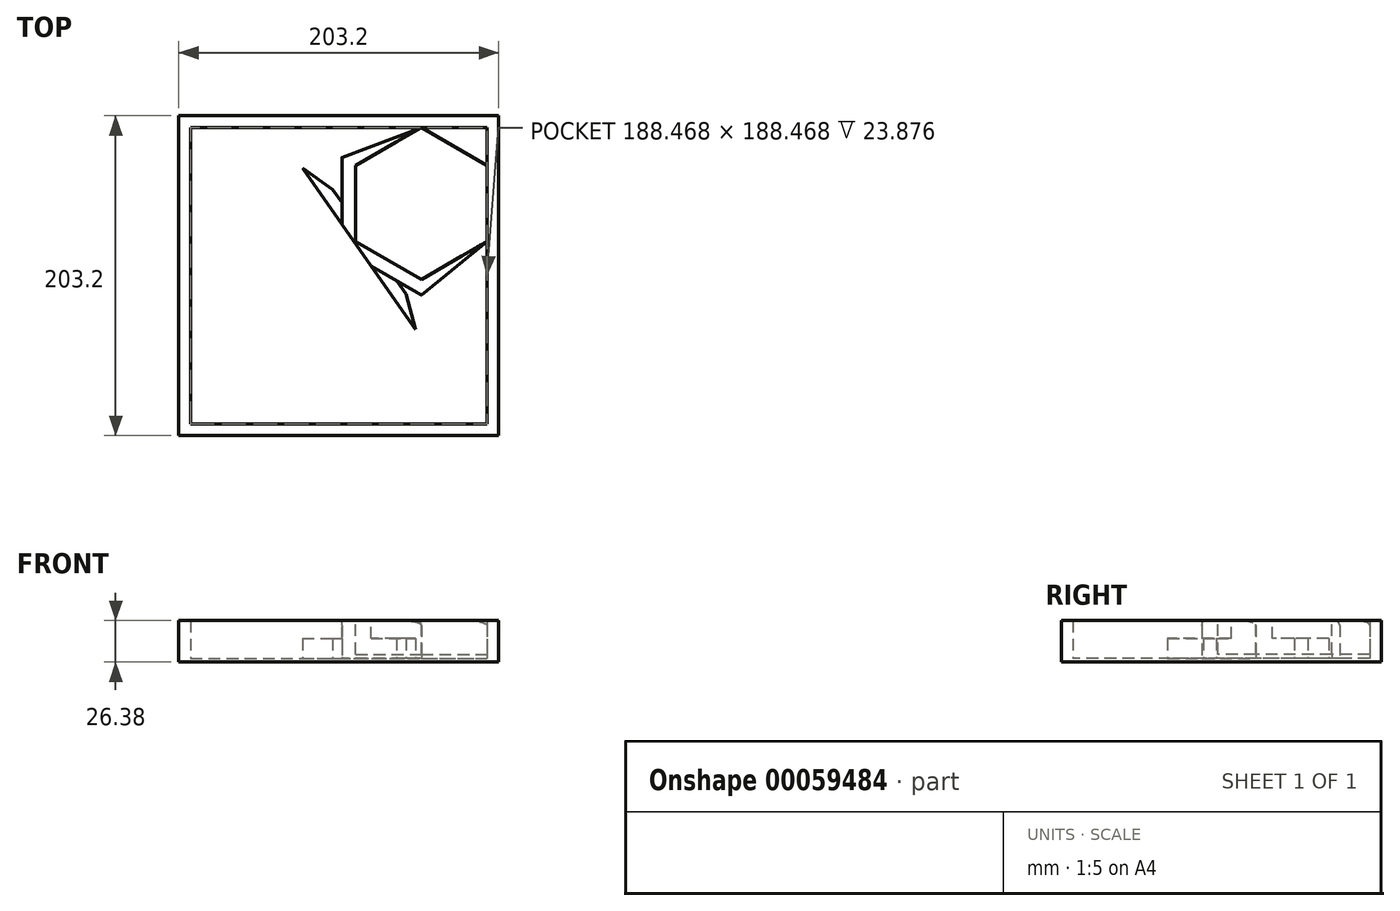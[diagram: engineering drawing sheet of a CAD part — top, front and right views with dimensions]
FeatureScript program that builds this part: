
annotation { "Feature Type Name" : "Feature", "Feature Type Description" : "" }
export const myFeature = defineFeature(function(context is Context, id is Id, definition is map)
    precondition{}
    {
        {
            var Q0;
            Q0=qCreatedBy(makeId("Top.planeOp"),FACE);
            var sketch = newSketch(context, id + "F0", { "sketchPlane" : qUnion([Q0])});
            skLineSegment(sketch, "E0.bottom", {"start": v(0, 0) * mm, "end": v(203.2, 0) * mm});
            skLineSegment(sketch, "E0.top", {"start": v(0, 203.2) * mm, "end": v(203.2, 203.2) * mm});
            skLineSegment(sketch, "E0.left", {"start": v(0, 0) * mm, "end": v(0, 203.2) * mm});
            skLineSegment(sketch, "E0.right", {"start": v(203.2, 0) * mm, "end": v(203.2, 203.2) * mm});
            skSolve(sketch);
        }
        {
            var Q0;
            Q0 = qSketchRegion(id + "F0", true);
            extrude(context, id + "F1", {"entities" : qUnion([Q0]), "depth" : 2.5 * mm});
        }
        {
            var Q0;
            Q0=makeQuery(id+"F1.opExtrude","CAP_FACE",FACE,{"disambiguationData":[OSD([sQuery(id+"F0.wireOp",EDGE,"E0.bottom"),sQuery(id+"F0.wireOp",EDGE,"E0.top"),sQuery(id+"F0.wireOp",EDGE,"E0.left"),sQuery(id+"F0.wireOp",EDGE,"E0.right")])],"isStart":false});
            var sketch = newSketch(context, id + "F2", { "sketchPlane" : qUnion([Q0])});
            skLineSegment(sketch, "E1.bottom", {"start": v(0, 203.2) * mm, "end": v(203.2, 203.2) * mm});
            skLineSegment(sketch, "E1.top", {"start": v(0, 0) * mm, "end": v(203.2, 0) * mm});
            skLineSegment(sketch, "E1.left", {"start": v(0, 203.2) * mm, "end": v(0, 0) * mm});
            skLineSegment(sketch, "E1.right", {"start": v(203.2, 203.2) * mm, "end": v(203.2, 0) * mm});
            skLineSegment(sketch, "E2.bottom", {"start": v(7.37, 195.83) * mm, "end": v(195.83, 195.83) * mm});
            skLineSegment(sketch, "E2.top", {"start": v(7.37, 7.37) * mm, "end": v(195.83, 7.37) * mm});
            skLineSegment(sketch, "E2.left", {"start": v(7.37, 195.83) * mm, "end": v(7.37, 7.37) * mm});
            skLineSegment(sketch, "E2.right", {"start": v(195.83, 195.83) * mm, "end": v(195.83, 7.37) * mm});
            skSolve(sketch);
        }
        {
            var Q0;
            Q0 = qSketchRegion(id + "F2", true);
            extrude(context, id + "F3", {"entities" : qUnion([Q0]), "operationType" : NewBodyOperationType.ADD, "depth" : 23.88 * mm});
        }
        {
            var Q0;
            Q0=makeQuery(id+"F1.opExtrude","CAP_FACE",FACE,{"disambiguationData":[OSD([sQuery(id+"F0.wireOp",EDGE,"E0.bottom"),sQuery(id+"F0.wireOp",EDGE,"E0.top"),sQuery(id+"F0.wireOp",EDGE,"E0.left"),sQuery(id+"F0.wireOp",EDGE,"E0.right")])],"isStart":false});
            var sketch = newSketch(context, id + "F4", { "sketchPlane" : qUnion([Q0])});
            skCircle(sketch, "E3.cCircle", {"center": v(154.04, 147.57) * mm, "radius": 41.8 * mm, "construction": true});
            skLineSegment(sketch, "E3.0", {"start": v(195.83, 171.7) * mm, "end": v(195.83, 123.44) * mm});
            skLineSegment(sketch, "E3.1", {"start": v(195.83, 123.44) * mm, "end": v(154.04, 99.31) * mm, "construction": true});
            skLineSegment(sketch, "E3.2", {"start": v(154.04, 99.31) * mm, "end": v(112.25, 123.44) * mm, "construction": true});
            skLineSegment(sketch, "E3.3", {"start": v(112.25, 123.44) * mm, "end": v(112.25, 171.7) * mm, "construction": true});
            skLineSegment(sketch, "E3.4", {"start": v(112.25, 171.7) * mm, "end": v(154.04, 195.83) * mm, "construction": true});
            skLineSegment(sketch, "E3.5", {"start": v(154.04, 195.83) * mm, "end": v(195.83, 171.7) * mm});
            skPoint(sketch, "E3.0.midPoint", {"position": v(195.83, 147.57) * mm});
            skLineSegment(sketch, "E4", {"start": v(154.04, 195.83) * mm, "end": v(103.58, 176.7) * mm});
            skLineSegment(sketch, "E5", {"start": v(103.58, 176.7) * mm, "end": v(112.25, 123.44) * mm, "construction": true});
            skLineSegment(sketch, "E6", {"start": v(112.25, 123.44) * mm, "end": v(154.04, 89.31) * mm, "construction": true});
            skLineSegment(sketch, "E7", {"start": v(154.04, 89.31) * mm, "end": v(195.83, 123.44) * mm});
            skLineSegment(sketch, "E8", {"start": v(78.53, 169.85) * mm, "end": v(150.23, 67.46) * mm});
            skLineSegment(sketch, "E9", {"start": v(195.83, 7.37) * mm, "end": v(7.37, 7.37) * mm, "construction": true});
            skLineSegment(sketch, "E10", {"start": v(7.37, 7.37) * mm, "end": v(7.37, 195.83) * mm, "construction": true});
            skLineSegment(sketch, "E11", {"start": v(78.53, 169.85) * mm, "end": v(97.69, 156.44) * mm});
            skLineSegment(sketch, "E12", {"start": v(97.69, 156.44) * mm, "end": v(109.66, 139.34) * mm});
            skLineSegment(sketch, "E13", {"start": v(150.23, 67.46) * mm, "end": v(144.17, 90.05) * mm});
            skLineSegment(sketch, "E14", {"start": v(144.17, 90.05) * mm, "end": v(132.2, 107.15) * mm});
            skLineSegment(sketch, "E15", {"start": v(109.66, 139.34) * mm, "end": v(103.58, 176.7) * mm, "construction": true});
            skLineSegment(sketch, "E16", {"start": v(132.2, 107.15) * mm, "end": v(154.04, 89.31) * mm, "construction": true});
            skLineSegment(sketch, "E17", {"start": v(154.04, 89.31) * mm, "end": v(138.34, 98.38) * mm});
            skLineSegment(sketch, "E18", {"start": v(103.58, 176.7) * mm, "end": v(103.58, 148.02) * mm});
            skSolve(sketch);
        }
        {
            var Q0;
            Q0 = qSketchRegion(id + "F4", true);
            extrude(context, id + "F5", {"entities" : qUnion([Q0]), "depth" : 23.88 * mm});
        }
        {
            var Q0;
            Q0=makeQuery(id+"F5.opExtrude","CAP_FACE",FACE,{"disambiguationData":[OSD([sQuery(id+"F4.wireOp",EDGE,"E3.0"),sQuery(id+"F4.wireOp",EDGE,"E3.5"),sQuery(id+"F4.wireOp",EDGE,"E4"),sQuery(id+"F4.wireOp",EDGE,"E7"),sQuery(id+"F4.wireOp",EDGE,"E8"),sQuery(id+"F4.wireOp",EDGE,"E11"),sQuery(id+"F4.wireOp",EDGE,"E12"),sQuery(id+"F4.wireOp",EDGE,"E13"),sQuery(id+"F4.wireOp",EDGE,"E14"),sQuery(id+"F4.wireOp",EDGE,"E15"),sQuery(id+"F4.wireOp",EDGE,"E16")])],"isStart":false});
            var sketch = newSketch(context, id + "F6", { "sketchPlane" : qUnion([Q0])});
            skCircle(sketch, "E19.cCircle", {"center": v(154.04, 147.57) * mm, "radius": 41.8 * mm, "construction": true});
            skPoint(sketch, "E19.cCircle.perimeterSnap0", {"position": v(174.94, 183.77) * mm});
            skLineSegment(sketch, "E19.0", {"start": v(154.04, 195.83) * mm, "end": v(195.83, 171.7) * mm});
            skLineSegment(sketch, "E19.1", {"start": v(195.83, 171.7) * mm, "end": v(195.83, 123.44) * mm});
            skLineSegment(sketch, "E19.2", {"start": v(195.83, 123.44) * mm, "end": v(154.04, 99.31) * mm});
            skLineSegment(sketch, "E19.3", {"start": v(154.04, 99.31) * mm, "end": v(112.25, 123.44) * mm});
            skLineSegment(sketch, "E19.4", {"start": v(112.25, 123.44) * mm, "end": v(112.25, 171.7) * mm});
            skLineSegment(sketch, "E19.5", {"start": v(112.25, 171.7) * mm, "end": v(154.04, 195.83) * mm});
            skPoint(sketch, "E19.0.midPoint", {"position": v(174.94, 183.77) * mm});
            skPoint(sketch, "E19.0.midPoint.positionSnap0", {"position": v(174.94, 183.77) * mm});
            skSolve(sketch);
        }
        {
            var Q0;
            Q0 = qSketchRegion(id + "F6", true);
            extrude(context, id + "F7", {"entities" : qUnion([Q0]), "operationType" : NewBodyOperationType.REMOVE, "oppositeDirection" : true, "depth" : 21.34 * mm});
        }
        {
            var Q0;
            Q0=makeQuery(id+"F5.opExtrude","CAP_FACE",FACE,{"disambiguationData":[OSD([sQuery(id+"F4.wireOp",EDGE,"E3.0"),sQuery(id+"F4.wireOp",EDGE,"E3.5"),sQuery(id+"F4.wireOp",EDGE,"E4"),sQuery(id+"F4.wireOp",EDGE,"E7"),sQuery(id+"F4.wireOp",EDGE,"E8"),sQuery(id+"F4.wireOp",EDGE,"E11"),sQuery(id+"F4.wireOp",EDGE,"E12"),sQuery(id+"F4.wireOp",EDGE,"E13"),sQuery(id+"F4.wireOp",EDGE,"E14"),sQuery(id+"F4.wireOp",EDGE,"E17"),sQuery(id+"F4.wireOp",EDGE,"E18")])],"isStart":false});
            var sketch = newSketch(context, id + "F8", { "sketchPlane" : qUnion([Q0])});
            skLineSegment(sketch, "E20", {"start": v(78.53, 169.85) * mm, "end": v(97.69, 156.44) * mm});
            skLineSegment(sketch, "E21", {"start": v(97.69, 156.44) * mm, "end": v(103.58, 148.02) * mm});
            skLineSegment(sketch, "E22", {"start": v(103.58, 148.02) * mm, "end": v(103.58, 134.07) * mm});
            skLineSegment(sketch, "E23", {"start": v(103.58, 134.07) * mm, "end": v(78.53, 169.85) * mm});
            skLineSegment(sketch, "E24", {"start": v(150.23, 67.46) * mm, "end": v(144.17, 90.05) * mm});
            skLineSegment(sketch, "E25", {"start": v(144.17, 90.05) * mm, "end": v(138.34, 98.38) * mm});
            skLineSegment(sketch, "E26", {"start": v(138.34, 98.38) * mm, "end": v(121.95, 107.84) * mm});
            skLineSegment(sketch, "E27", {"start": v(121.95, 107.84) * mm, "end": v(150.23, 67.46) * mm});
            skSolve(sketch);
        }
        {
            var Q0;
            Q0 = qSketchRegion(id + "F8", true);
            extrude(context, id + "F9", {"entities" : qUnion([Q0]), "operationType" : NewBodyOperationType.REMOVE, "oppositeDirection" : true, "depth" : 11.43 * mm});
        }
        {
            var Q0;
            Q0=makeQuery(id+"F9.boolean.opBoolean","MERGE",EDGE,{"derivedFrom":[makeQuery(id+"F5.opExtrude","CAP_EDGE",EDGE,{"disambiguationData":[OSD([sQuery(id+"F4.wireOp",EDGE,"E18")])],"isStart":false}),makeQuery(id+"F9.opExtrude","CAP_EDGE",EDGE,{"disambiguationData":[OSD([sQuery(id+"F8.wireOp",EDGE,"E22")])],"isStart":true})]});
            var Q1;
            Q1=makeQuery(id+"F9.boolean.opBoolean","MERGE",EDGE,{"derivedFrom":[makeQuery(id+"F5.opExtrude","CAP_EDGE",EDGE,{"disambiguationData":[OSD([sQuery(id+"F4.wireOp",EDGE,"E17")])],"isStart":false}),makeQuery(id+"F9.opExtrude","CAP_EDGE",EDGE,{"disambiguationData":[OSD([sQuery(id+"F8.wireOp",EDGE,"E26")])],"isStart":true})]});
            var Q2;
            Q2=makeQuery(id+"F5.opExtrude","CAP_EDGE",EDGE,{"disambiguationData":[OSD([sQuery(id+"F4.wireOp",EDGE,"E7")])],"isStart":false});
            var Q3;
            Q3=makeQuery(id+"F5.opExtrude","CAP_EDGE",EDGE,{"disambiguationData":[OSD([sQuery(id+"F4.wireOp",EDGE,"E4")])],"isStart":false});
            var Q4;
            Q4=makeQuery(id+"F9.boolean.opBoolean","COPY",EDGE,{"derivedFrom":makeQuery(id+"F9.opExtrude","CAP_EDGE",EDGE,{"disambiguationData":[OSD([sQuery(id+"F8.wireOp",EDGE,"E20")])],"isStart":false})});
            var Q5;
            Q5=makeQuery(id+"F9.boolean.opBoolean","COPY",EDGE,{"derivedFrom":makeQuery(id+"F9.opExtrude","CAP_EDGE",EDGE,{"disambiguationData":[OSD([sQuery(id+"F8.wireOp",EDGE,"E24")])],"isStart":false})});
            var Q6;
            Q6=makeQuery(id+"F9.boolean.opBoolean","COPY",EDGE,{"derivedFrom":makeQuery(id+"F9.opExtrude","CAP_EDGE",EDGE,{"disambiguationData":[OSD([sQuery(id+"F8.wireOp",EDGE,"E25")])],"isStart":false})});
            var Q7;
            Q7=makeQuery(id+"F9.boolean.opBoolean","COPY",EDGE,{"derivedFrom":makeQuery(id+"F9.opExtrude","CAP_EDGE",EDGE,{"disambiguationData":[OSD([sQuery(id+"F8.wireOp",EDGE,"E21")])],"isStart":false})});
            fillet(context, id + "F10", {"entities" : qUnion([Q0, Q1, Q2, Q3, Q4, Q5, Q6, Q7]), "radius" : 3 * mm, "tangentPropagation" : true, "allowEdgeOverflow" : false});
        }
    });
